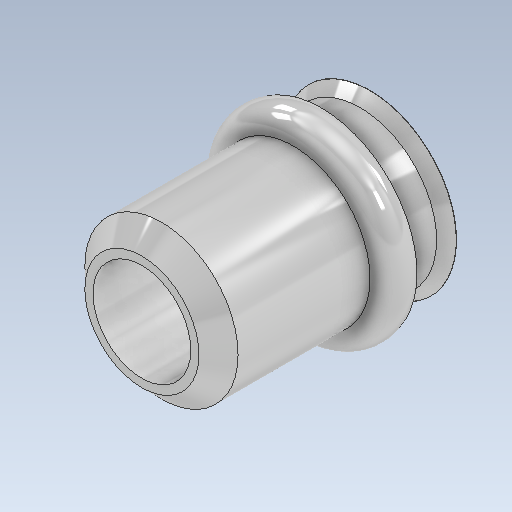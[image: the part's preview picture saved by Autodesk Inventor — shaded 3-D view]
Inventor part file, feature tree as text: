
AUTODESK INVENTOR PART (.ipt)
format: ipt  version: 2021 (Build 250183000, 183)  size: 202,752 bytes
history: native  units: mm
features: sketch x6, extrude x4, chamfer x2, projected_geometry x2, plane x1, sweep x1
ambient origin geometry x8: Origin, YZ Plane, XZ Plane, XY Plane, X Axis, Y Axis, Z Axis, Center Point
bodies: Solid1 (feature_tree)
feature tree (16):
  extrude  "Extrusion1"  Depth=7.0mm TaperAngle=0.0deg
  chamfer  "Chamfer1"  Distance=0.6mm Angle=45.0deg
  extrude  "Extrusion2"  TaperAngle=0.0deg  [1 undecoded]
  extrude  "Extrusion3"  Depth=5.3mm
  chamfer  "Chamfer2"  Distance=0.3mm Angle=45.0deg
  extrude  "Extrusion4"  [1 undecoded]
  plane  "Work Plane1"
  sweep  "Sweep1"
  sketch  "Sketch1"  dims[d0=4.7mm d1=7.0mm d2=0.0mm d3=0.6mm d4=2.0mm d5=45.0deg]
  sketch  "Sketch2"  dims[d6=3.0mm d7=0.0mm d8=0.0mm]
  sketch  "Sketch3"  dims[d9=0.01mm d10=0.0mm d11=5.3mm d12=0.3mm d13=2.0mm d14=45.0deg]
  sketch  "Sketch4"  dims[d15=0.0mm d16=0.0mm d17=-1.5mm]
  projected_geometry  "Projected Loop1"
  sketch  "Sketch5"  dims[d18=3.0mm d19=0.0mm d20=0.0mm]
  projected_geometry  "Projected Loop2"
  sketch  "Sketch6"
note: 2 required parameter values undecoded (feature->parameter linkage not recoverable at this tier; creation-order binding heuristic only, values carry confidence <= 0.55)
